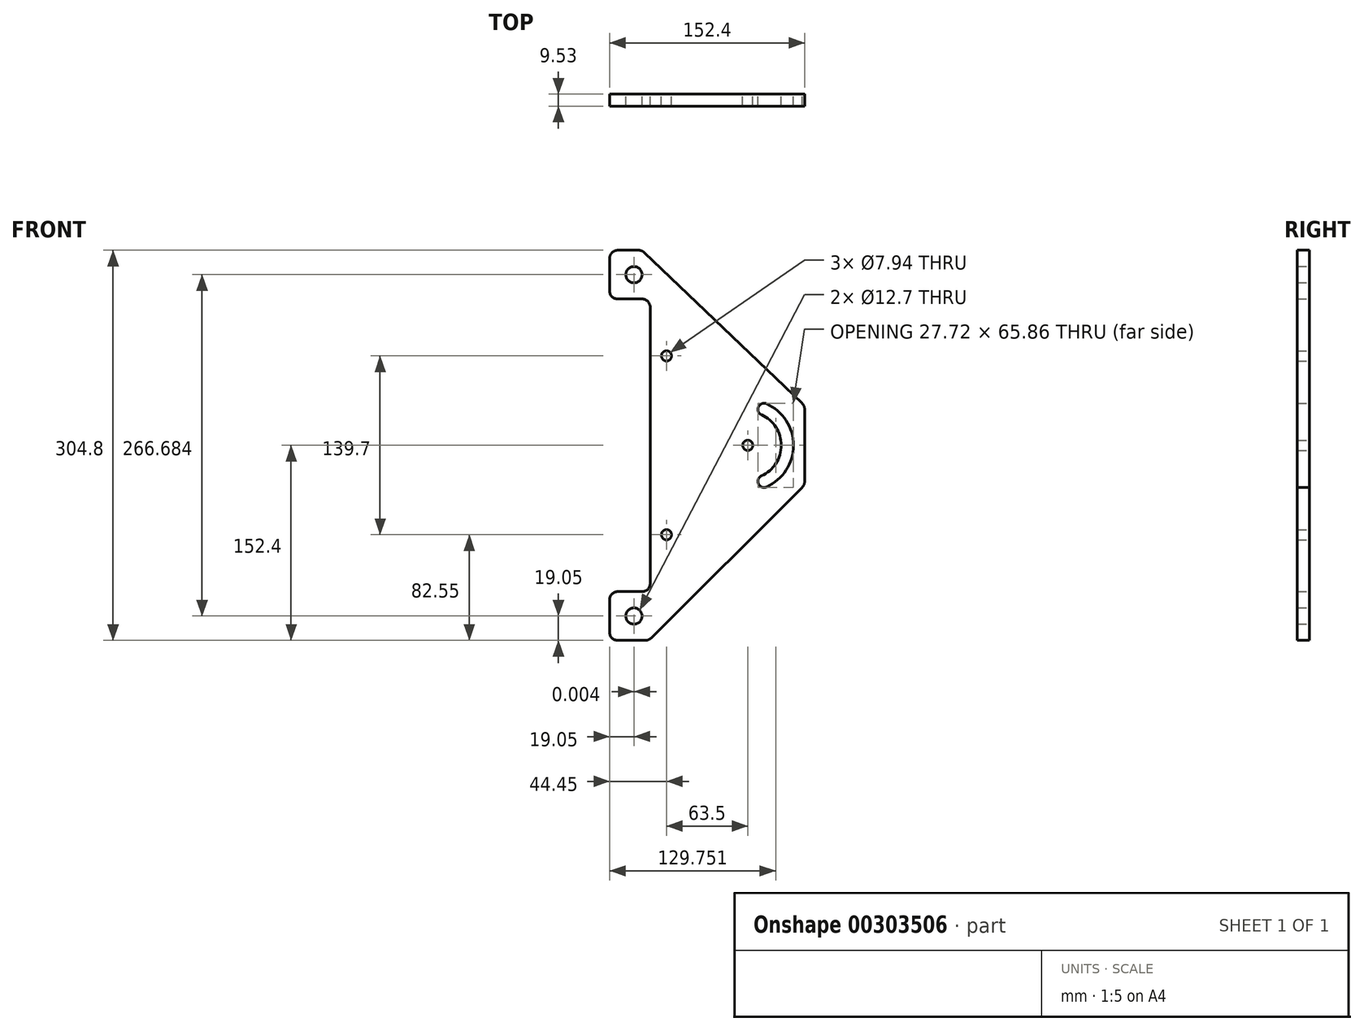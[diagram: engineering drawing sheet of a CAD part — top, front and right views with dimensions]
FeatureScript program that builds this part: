
annotation { "Feature Type Name" : "Feature", "Feature Type Description" : "" }
export const myFeature = defineFeature(function(context is Context, id is Id, definition is map)
    precondition{}
    {
        {
            var Q0;
            Q0=qCreatedBy(makeId("Front.planeOp"),FACE);
            var sketch = newSketch(context, id + "F0", { "sketchPlane" : qUnion([Q0])});
            skLineSegment(sketch, "E0.right", {"start": v(76.2, 28.17) * mm, "end": v(76.2, -28.17) * mm});
            skPoint(sketch, "E0.middle", {"position": v(0, 0) * mm});
            skPoint(sketch, "E1.visualSharp", {"position": v(-76.2, -152.4) * mm});
            skPoint(sketch, "E2.visualSharp", {"position": v(76.2, -152.4) * mm});
            skPoint(sketch, "E3.visualSharp", {"position": v(76.2, 152.4) * mm});
            skPoint(sketch, "E4.visualSharp", {"position": v(-76.2, 152.4) * mm});
            skPoint(sketch, "E5.visualSharp", {"position": v(-45.72, -152.4) * mm});
            skArc(sketch, "E6.filletArc", {"start": v(74.23, -32.77) * mm, "mid": v(75.69, -30.67) * mm, "end": v(76.2, -28.17) * mm});
            skArc(sketch, "E7.filletArc", {"start": v(76.2, 28.17) * mm, "mid": v(75.69, 30.66) * mm, "end": v(74.24, 32.76) * mm});
            skPoint(sketch, "E8.visualSharp", {"position": v(-50.8, 152.4) * mm});
            skLineSegment(sketch, "E9.trimOffspring", {"start": v(-50.97, 152.4) * mm, "end": v(-50.8, 152.4) * mm});
            skCircle(sketch, "E10", {"center": v(-57.15, 133.33) * mm, "radius": 6.35 * mm});
            skCircle(sketch, "E11", {"center": v(-57.15, -133.35) * mm, "radius": 6.35 * mm});
            skLineSegment(sketch, "E12", {"start": v(-44.45, 107.95) * mm, "end": v(-44.45, -107.95) * mm});
            skLineSegment(sketch, "E13", {"start": v(-50.8, 114.3) * mm, "end": v(-69.85, 114.3) * mm});
            skLineSegment(sketch, "E14", {"start": v(-50.8, -114.3) * mm, "end": v(-69.85, -114.3) * mm});
            skArc(sketch, "E15.filletArc", {"start": v(-76.2, 120.65) * mm, "mid": v(-74.34, 116.16) * mm, "end": v(-69.85, 114.3) * mm});
            skPoint(sketch, "E16.visualSharp", {"position": v(-44.45, 114.3) * mm});
            skArc(sketch, "E16.filletArc", {"start": v(-44.45, 107.95) * mm, "mid": v(-46.3, 112.44) * mm, "end": v(-50.8, 114.3) * mm});
            skPoint(sketch, "E17.visualSharp", {"position": v(-44.45, -114.3) * mm});
            skArc(sketch, "E17.filletArc", {"start": v(-50.8, -114.3) * mm, "mid": v(-46.31, -112.44) * mm, "end": v(-44.45, -107.95) * mm});
            skPoint(sketch, "E18.visualSharp", {"position": v(-63.5, -114.3) * mm});
            skArc(sketch, "E18.filletArc", {"start": v(-69.85, -114.3) * mm, "mid": v(-74.34, -116.16) * mm, "end": v(-76.2, -120.65) * mm});
            skLineSegment(sketch, "E19", {"start": v(-76.2, 120.65) * mm, "end": v(-76.2, 146.05) * mm});
            skLineSegment(sketch, "E20", {"start": v(-69.85, 152.4) * mm, "end": v(-53.43, 152.4) * mm});
            skLineSegment(sketch, "E21", {"start": v(74.24, 32.76) * mm, "end": v(-49.04, 150.64) * mm});
            skArc(sketch, "E22.filletArc", {"start": v(-69.85, 152.4) * mm, "mid": v(-74.34, 150.54) * mm, "end": v(-76.2, 146.05) * mm});
            skArc(sketch, "E23.filletArc", {"start": v(-49.04, 150.64) * mm, "mid": v(-51.07, 151.94) * mm, "end": v(-53.43, 152.4) * mm});
            skLineSegment(sketch, "E24", {"start": v(-76.2, -120.65) * mm, "end": v(-76.2, -146.05) * mm});
            skLineSegment(sketch, "E25", {"start": v(-48.35, -152.4) * mm, "end": v(-69.85, -152.4) * mm});
            skLineSegment(sketch, "E26", {"start": v(-43.86, -150.55) * mm, "end": v(74.23, -32.77) * mm});
            skArc(sketch, "E27.filletArc", {"start": v(-76.2, -146.05) * mm, "mid": v(-74.34, -150.54) * mm, "end": v(-69.85, -152.4) * mm});
            skArc(sketch, "E28.filletArc", {"start": v(-48.35, -152.4) * mm, "mid": v(-45.92, -151.92) * mm, "end": v(-43.86, -150.55) * mm});
            skPoint(sketch, "E29", {"position": v(-31.74, 69.85) * mm});
            skPoint(sketch, "E30", {"position": v(-31.75, -69.85) * mm});
            skArc(sketch, "E31", {"start": v(46.4, 32.51) * mm, "mid": v(40.1, 30.13) * mm, "end": v(42.5, 23.83) * mm});
            skArc(sketch, "E32", {"start": v(42.5, -23.83) * mm, "mid": v(40.1, -30.13) * mm, "end": v(46.4, -32.51) * mm});
            skArc(sketch, "E33", {"start": v(46.4, -32.51) * mm, "mid": v(67.41, 0) * mm, "end": v(46.4, 32.51) * mm});
            skArc(sketch, "E34", {"start": v(42.5, -23.83) * mm, "mid": v(57.89, 0) * mm, "end": v(42.5, 23.83) * mm});
            skSolve(sketch);
        }
        {
            var Q0;
            Q0=makeQuery(id+"F0.imprint","IMPRINT",FACE,{"disambiguationData":[TD([[makeQuery(id+"F0.imprint","IMPRINT",EDGE,{"derivedFrom":sQuery(id+"F0.wireOp",EDGE,"E0.right")}),-1.0]])]});
            extrude(context, id + "F1", {"entities" : qUnion([Q0]), "depth" : 9.52 * mm});
        }
        {
            var Q0;
            Q0=sQuery(id+"F0.wireOp",VERTEX,"E33.center");
            var Q1;
            Q1=sQuery(id+"F0.wireOp",VERTEX,"E29");
            var Q2;
            Q2=sQuery(id+"F0.wireOp",VERTEX,"E30");
            var Q3;
            Q3=makeQuery(id+"F1.opExtrude","SWEPT_BODY",BODY,{"disambiguationData":[OSD([sQuery(id+"F0.wireOp",EDGE,"E0.right"),sQuery(id+"F0.wireOp",EDGE,"ZYUntrGx-CoeK-2xTB-2XOE-j7YhSFoO4wcg"),sQuery(id+"F0.wireOp",EDGE,"Np3mL0nf-s7Iy-KZKR-OzV8-bdhjjrdxYraP"),sQuery(id+"F0.wireOp",EDGE,"DFBYPZKz-oMP7-7fVi-sFtP-IjV6AERX70mg"),sQuery(id+"F0.wireOp",EDGE,"E6.filletArc"),sQuery(id+"F0.wireOp",EDGE,"E7.filletArc"),sQuery(id+"F0.wireOp",EDGE,"Zquak6TD-LLTB-N72V-6rFh-hohHIUOfQQcE"),sQuery(id+"F0.wireOp",EDGE,"E10"),sQuery(id+"F0.wireOp",EDGE,"E11"),sQuery(id+"F0.wireOp",EDGE,"E12"),sQuery(id+"F0.wireOp",EDGE,"E13"),sQuery(id+"F0.wireOp",EDGE,"E14"),sQuery(id+"F0.wireOp",EDGE,"E15.filletArc"),sQuery(id+"F0.wireOp",EDGE,"E16.filletArc"),sQuery(id+"F0.wireOp",EDGE,"E17.filletArc"),sQuery(id+"F0.wireOp",EDGE,"E18.filletArc"),sQuery(id+"F0.wireOp",EDGE,"E19"),sQuery(id+"F0.wireOp",EDGE,"E20"),sQuery(id+"F0.wireOp",EDGE,"E21"),sQuery(id+"F0.wireOp",EDGE,"E22.filletArc"),sQuery(id+"F0.wireOp",EDGE,"E23.filletArc"),sQuery(id+"F0.wireOp",EDGE,"E24"),sQuery(id+"F0.wireOp",EDGE,"E25"),sQuery(id+"F0.wireOp",EDGE,"E26"),sQuery(id+"F0.wireOp",EDGE,"E27.filletArc"),sQuery(id+"F0.wireOp",EDGE,"E28.filletArc")])]});
            hole(context, id + "F2", {"style" : HoleStyle.SIMPLE, "endStyle" : HoleEndStyle.THROUGH, "oppositeDirection" : true, "standardTappedOrClearance" : lookupTablePath({ "standard" : "ANSI", "engagement" : "75%", "pitch" : "16 tpi", "size" : "3/8", "type" : "Tapped" }), "standardBlindInLast" : lookupTablePath({ "standard" : "ANSI", "engagement" : "75%", "pitch" : "16 tpi", "size" : "3/8", "type" : "Tapped" }), "holeDiameter" : 7.94 * mm, "showTappedDepth" : true, "tappedDepth" : 12.7 * mm, "tapClearance" : 3, "locations" : qUnion([Q0, Q1, Q2]), "scope" : qUnion([Q3]), "majorDiameter" : 9.53 * mm});
        }
    });
